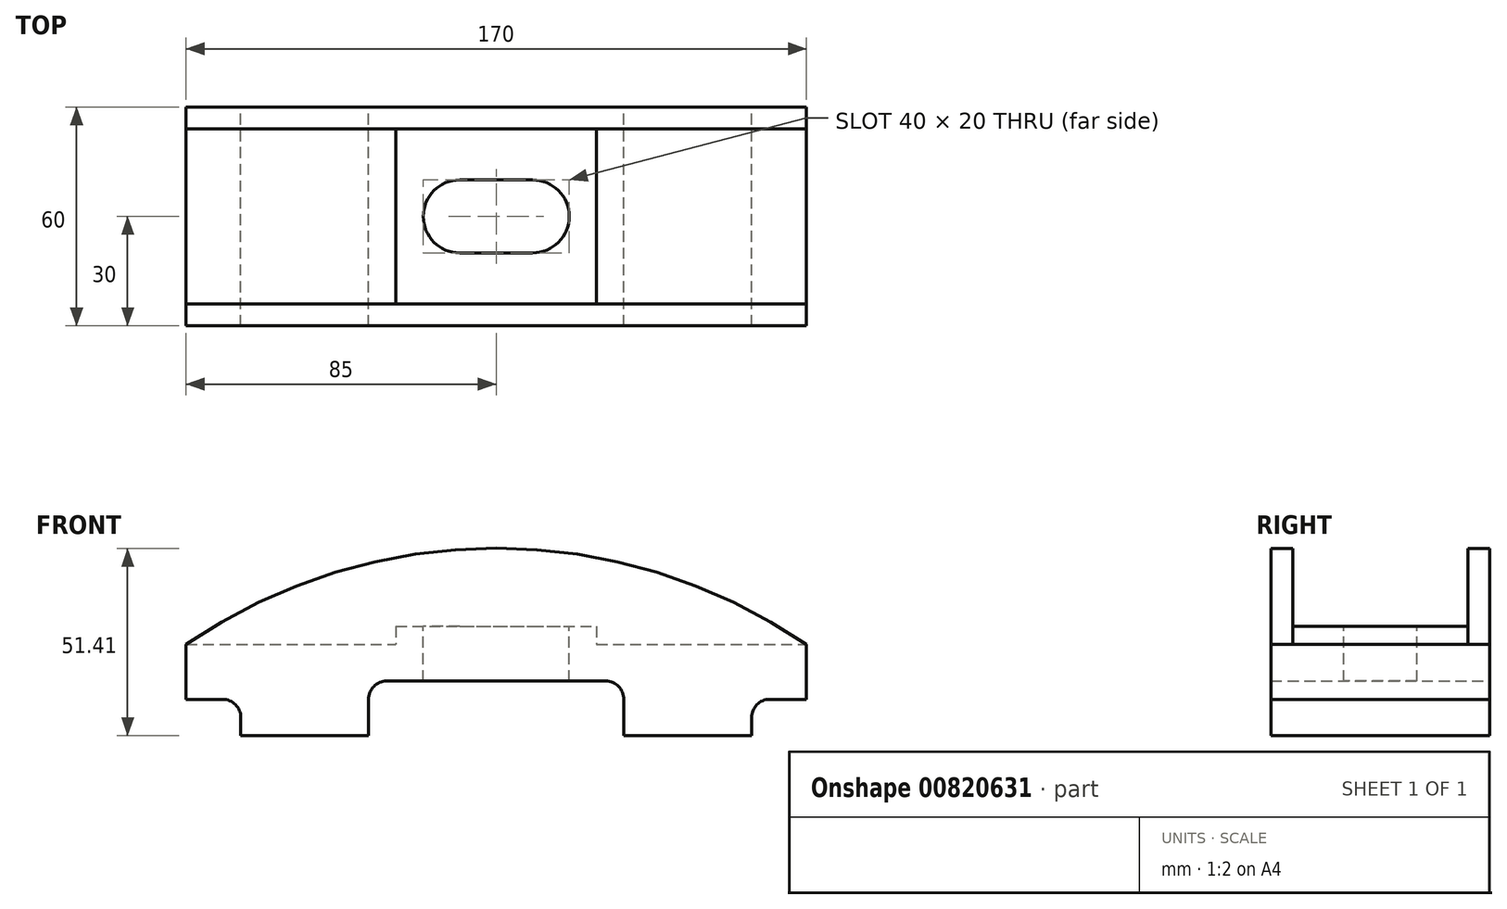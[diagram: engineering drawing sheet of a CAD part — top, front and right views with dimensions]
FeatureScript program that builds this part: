
annotation { "Feature Type Name" : "Feature", "Feature Type Description" : "" }
export const myFeature = defineFeature(function(context is Context, id is Id, definition is map)
    precondition{}
    {
        {
            var Q0;
            Q0=qCreatedBy(makeId("Front.planeOp"),FACE);
            var sketch = newSketch(context, id + "F0", { "sketchPlane" : qUnion([Q0])});
            skLineSegment(sketch, "E0.bottom", {"start": v(-70, -12.5) * mm, "end": v(-35, -12.5) * mm});
            skLineSegment(sketch, "E0.top", {"start": v(-85, 12.5) * mm, "end": v(85, 12.5) * mm});
            skLineSegment(sketch, "E0.left", {"start": v(-85, -2.5) * mm, "end": v(-85, 12.5) * mm});
            skLineSegment(sketch, "E0.right", {"start": v(85, -2.5) * mm, "end": v(85, 12.5) * mm});
            skPoint(sketch, "E0.middle", {"position": v(0, 0) * mm});
            skLineSegment(sketch, "E1", {"start": v(-70, -12.5) * mm, "end": v(-70, -7.5) * mm});
            skLineSegment(sketch, "E2", {"start": v(-75, -2.5) * mm, "end": v(-85, -2.5) * mm});
            skLineSegment(sketch, "E3", {"start": v(70, -12.5) * mm, "end": v(70, -7.5) * mm});
            skLineSegment(sketch, "E4", {"start": v(75, -2.5) * mm, "end": v(85, -2.5) * mm});
            skPoint(sketch, "E5.orphan", {"position": v(-85, -12.5) * mm});
            skPoint(sketch, "E6.orphan", {"position": v(85, -12.5) * mm});
            skLineSegment(sketch, "E7", {"start": v(35, -12.5) * mm, "end": v(70, -12.5) * mm});
            skLineSegment(sketch, "E8", {"start": v(-35, -12.5) * mm, "end": v(-35, -2.5) * mm});
            skLineSegment(sketch, "E9", {"start": v(-30, 2.5) * mm, "end": v(30, 2.5) * mm});
            skLineSegment(sketch, "E10", {"start": v(35, -2.5) * mm, "end": v(35, -12.5) * mm});
            skPoint(sketch, "E11.visualSharp", {"position": v(-70, -2.5) * mm});
            skArc(sketch, "E11.filletArc", {"start": v(-70, -7.5) * mm, "mid": v(-71.46, -3.96) * mm, "end": v(-75, -2.5) * mm});
            skPoint(sketch, "E12.visualSharp", {"position": v(-35, 2.5) * mm});
            skArc(sketch, "E12.filletArc", {"start": v(-30, 2.5) * mm, "mid": v(-33.54, 1.04) * mm, "end": v(-35, -2.5) * mm});
            skPoint(sketch, "E13.visualSharp", {"position": v(35, 2.5) * mm});
            skArc(sketch, "E13.filletArc", {"start": v(35, -2.5) * mm, "mid": v(33.54, 1.04) * mm, "end": v(30, 2.5) * mm});
            skPoint(sketch, "E14.visualSharp", {"position": v(70, -2.5) * mm});
            skArc(sketch, "E14.filletArc", {"start": v(75, -2.5) * mm, "mid": v(71.46, -3.96) * mm, "end": v(70, -7.5) * mm});
            skArc(sketch, "E15", {"start": v(85, 12.5) * mm, "mid": v(0, 38.9) * mm, "end": v(-85, 12.5) * mm});
            skSolve(sketch);
        }
        {
            var Q0;
            Q0 = qSketchRegion(id + "F0", true);
            extrude(context, id + "F1", {"entities" : qUnion([Q0]), "depth" : 60 * mm, "offsetDistance" : 25.4 * mm});
        }
        {
            var Q0;
            Q0=makeQuery(id+"F1.opExtrude","SWEPT_FACE",FACE,{"disambiguationData":[OSD([sQuery(id+"F0.wireOp",EDGE,"E0.right")])]});
            var sketch = newSketch(context, id + "F2", { "sketchPlane" : qUnion([Q0])});
            skLineSegment(sketch, "E16", {"start": v(-60, 12.5) * mm, "end": v(-54, 12.5) * mm});
            skLineSegment(sketch, "E17", {"start": v(-54, 12.5) * mm, "end": v(-6, 12.5) * mm});
            skLineSegment(sketch, "E18", {"start": v(-6, 12.5) * mm, "end": v(0, 12.5) * mm});
            skLineSegment(sketch, "E19.top", {"start": v(-54, 41.12) * mm, "end": v(-6, 41.12) * mm});
            skLineSegment(sketch, "E19.left", {"start": v(-54, 12.5) * mm, "end": v(-54, 41.12) * mm});
            skLineSegment(sketch, "E19.right", {"start": v(-6, 12.5) * mm, "end": v(-6, 41.12) * mm});
            skSolve(sketch);
        }
        {
            var Q0;
            Q0 = qSketchRegion(id + "F2", true);
            extrude(context, id + "F3", {"entities" : qUnion([Q0]), "operationType" : NewBodyOperationType.REMOVE, "endBound" : BoundingType.THROUGH_ALL, "oppositeDirection" : true, "depth" : 25.4 * mm, "offsetDistance" : 25.4 * mm});
        }
        {
            var Q0;
            Q0=makeQuery(id+"F3.boolean.opBoolean","COPY",FACE,{"derivedFrom":makeQuery(id+"F3.opExtrude","SWEPT_FACE",FACE,{"disambiguationData":[OSD([sQuery(id+"F2.wireOp",EDGE,"E17")])]})});
            var sketch = newSketch(context, id + "F4", { "sketchPlane" : qUnion([Q0])});
            skLineSegment(sketch, "E20", {"start": v(-85, -54) * mm, "end": v(-27.5, -54) * mm});
            skLineSegment(sketch, "E21", {"start": v(-27.5, -54) * mm, "end": v(27.5, -54) * mm});
            skLineSegment(sketch, "E22", {"start": v(27.5, -54) * mm, "end": v(85, -54) * mm});
            skLineSegment(sketch, "E23", {"start": v(-27.5, -54) * mm, "end": v(-27.5, -6) * mm});
            skLineSegment(sketch, "E24", {"start": v(-27.5, -6) * mm, "end": v(27.5, -6) * mm});
            skLineSegment(sketch, "E25", {"start": v(27.5, -6) * mm, "end": v(27.5, -54) * mm});
            skSolve(sketch);
        }
        {
            var Q0;
            Q0 = qSketchRegion(id + "F4", true);
            extrude(context, id + "F5", {"entities" : qUnion([Q0]), "operationType" : NewBodyOperationType.ADD, "depth" : 5 * mm, "offsetDistance" : 25.4 * mm});
        }
        {
            var Q0;
            Q0=makeQuery(id+"F5.opExtrude","CAP_FACE",FACE,{"disambiguationData":[OSD([sQuery(id+"F4.wireOp",EDGE,"E21"),sQuery(id+"F4.wireOp",EDGE,"E23"),sQuery(id+"F4.wireOp",EDGE,"E24"),sQuery(id+"F4.wireOp",EDGE,"E25")])],"isStart":false});
            var sketch = newSketch(context, id + "F6", { "sketchPlane" : qUnion([Q0])});
            skLineSegment(sketch, "E26.bottom", {"start": v(-10, -40) * mm, "end": v(10, -40) * mm});
            skLineSegment(sketch, "E26.top", {"start": v(-10, -20) * mm, "end": v(10, -20) * mm});
            skLineSegment(sketch, "E26.left", {"start": v(-10, -40) * mm, "end": v(-10, -20) * mm});
            skLineSegment(sketch, "E26.right", {"start": v(10, -40) * mm, "end": v(10, -20) * mm});
            skPoint(sketch, "E26.middle", {"position": v(0, -30) * mm});
            skPoint(sketch, "E26.middle.positionSnap0", {"position": v(-27.5, -30) * mm});
            skPoint(sketch, "E26.centerSnap0", {"position": v(-27.5, -30) * mm});
            skCircle(sketch, "E27", {"center": v(-10, -30) * mm, "radius": 10 * mm});
            skCircle(sketch, "E28", {"center": v(10, -30) * mm, "radius": 10 * mm});
            skSolve(sketch);
        }
        {
            var Q0;
            Q0 = qSketchRegion(id + "F6", true);
            extrude(context, id + "F7", {"entities" : qUnion([Q0]), "operationType" : NewBodyOperationType.REMOVE, "endBound" : BoundingType.THROUGH_ALL, "oppositeDirection" : true, "depth" : 25.4 * mm, "offsetDistance" : 25.4 * mm});
        }
    });
